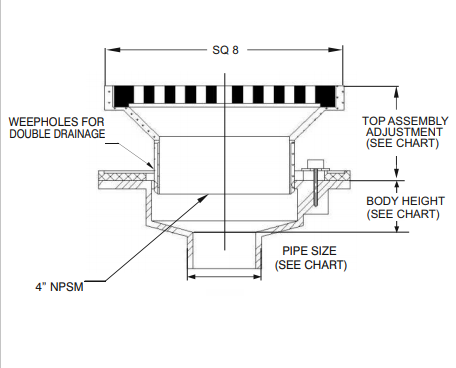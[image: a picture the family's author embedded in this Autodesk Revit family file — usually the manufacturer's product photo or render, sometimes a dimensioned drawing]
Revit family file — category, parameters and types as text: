
# Revit family: R1220-PR
name_source: partatom
category: Plumbing Fixtures
revit_build: Autodesk Revit 2018 (Build: 20170223_1515(x64)
units: mm (PartAtom-declared; Revit-internal decimal feet)

## family parameters
Cut with Voids When Loaded = No
Host = Face
Part Type = Normal
Room Calculation Point = No
Round Connector Dimension = Use Radius
Shared = No

## types (4) — shared parameters
Body Height = 0' - 6 1/2"
Default Elevation = 0' - 0"
Description = MEDIUM SUMP PROMENADE DECK DRAIN
Floor Drain Material = Paint - Sherwin Williams Paint - #952C2A - Bellwood Red
Manufacturer = MIFAB
Model = R1220-PR
URL = WWW.MIFAB.COM
zero-valued in all types: CWFU, WFU

## per-type parameters (varying)
| type | Pipe Diameter | Pipe Radius |
| 2" Drain Pipe Size | 0' - 2" | 0' - 1" |
| 3" Drain Pipe Size | 0' - 3" | 0' - 1 1/2" |
| 4" Drain Pipe Size | 0' - 4" | 0' - 2" |
| 6" Drain Pipe Size | 0' - 6" | 0' - 3" |

## geometry (parser evidence)
native form markers: Blend x3, Sweep x6
no freeform markers — native parametric forms only
